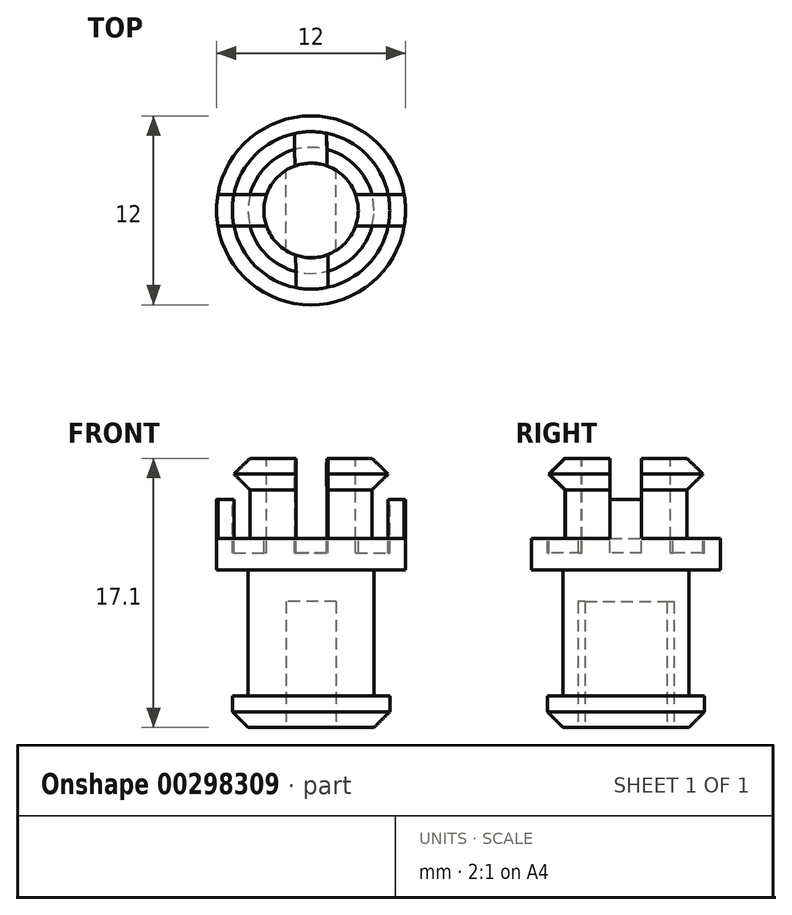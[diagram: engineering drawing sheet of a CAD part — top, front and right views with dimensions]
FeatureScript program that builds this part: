
annotation { "Feature Type Name" : "Feature", "Feature Type Description" : "" }
export const myFeature = defineFeature(function(context is Context, id is Id, definition is map)
    precondition{}
    {
        {
            var Q0;
            Q0=qCreatedBy(makeId("Top.planeOp"),FACE);
            var sketch = newSketch(context, id + "F0", { "sketchPlane" : qUnion([Q0])});
            skCircle(sketch, "E0", {"center": v(0, 0) * mm, "radius": 5 * mm});
            skSolve(sketch);
        }
        {
            var Q0;
            Q0 = qSketchRegion(id + "F0", true);
            extrude(context, id + "F1", {"entities" : qUnion([Q0]), "depth" : 2 * mm});
        }
        {
            var Q0;
            Q0=makeQuery(id+"F1.opExtrude","CAP_FACE",FACE,{"disambiguationData":[OSD([sQuery(id+"F0.wireOp",EDGE,"E0")])],"isStart":false});
            var sketch = newSketch(context, id + "F2", { "sketchPlane" : qUnion([Q0])});
            skCircle(sketch, "E1", {"center": v(0, 0) * mm, "radius": 4 * mm});
            skSolve(sketch);
        }
        {
            var Q0;
            Q0 = qSketchRegion(id + "F2", true);
            extrude(context, id + "F3", {"entities" : qUnion([Q0]), "operationType" : NewBodyOperationType.ADD, "depth" : 8 * mm});
        }
        {
            var Q0;
            Q0=makeQuery(id+"F3.opExtrude","CAP_FACE",FACE,{"disambiguationData":[OSD([sQuery(id+"F2.wireOp",EDGE,"E1")])],"isStart":false});
            var sketch = newSketch(context, id + "F4", { "sketchPlane" : qUnion([Q0])});
            skCircle(sketch, "E2", {"center": v(0, 0) * mm, "radius": 6 * mm});
            skSolve(sketch);
        }
        {
            var Q0;
            Q0 = qSketchRegion(id + "F4", true);
            extrude(context, id + "F5", {"entities" : qUnion([Q0]), "operationType" : NewBodyOperationType.ADD, "depth" : 2 * mm});
        }
        {
            var Q0;
            Q0=makeQuery(id+"F5.opExtrude","CAP_FACE",FACE,{"disambiguationData":[OSD([sQuery(id+"F4.wireOp",EDGE,"E2")])],"isStart":false});
            var sketch = newSketch(context, id + "F6", { "sketchPlane" : qUnion([Q0])});
            skCircle(sketch, "E3", {"center": v(0, 0) * mm, "radius": 4.15 * mm});
            skLineSegment(sketch, "E4", {"start": v(-5.92, 1) * mm, "end": v(-4.52, 1) * mm});
            skLineSegment(sketch, "E5.MirrorCS", {"start": v(5.92, 1) * mm, "end": v(4.52, 1) * mm});
            skLineSegment(sketch, "E6.MirrorCS", {"start": v(5.92, -1) * mm, "end": v(4.52, -1) * mm});
            skLineSegment(sketch, "E7.MirrorCS", {"start": v(-5.92, -1) * mm, "end": v(-4.52, -1) * mm});
            skLineSegment(sketch, "E8", {"start": v(-4.52, 1) * mm, "end": v(-4.52, -1) * mm});
            skLineSegment(sketch, "E9.MirrorCS", {"start": v(4.52, 1) * mm, "end": v(4.52, -1) * mm});
            skLineSegment(sketch, "E10", {"start": v(-4.03, 1) * mm, "end": v(4.03, 1) * mm});
            skLineSegment(sketch, "E11.MirrorCS", {"start": v(-4.03, -1) * mm, "end": v(4.03, -1) * mm});
            skLineSegment(sketch, "E12", {"start": v(-1, 4.03) * mm, "end": v(-1, -4.03) * mm});
            skLineSegment(sketch, "E13.MirrorCS", {"start": v(1, 4.03) * mm, "end": v(1, -4.03) * mm});
            skSolve(sketch);
        }
        {
            var Q0;
            {var subQ0=sQuery(id+"F6.wireOp",EDGE,"E5.MirrorCS");Q0=makeQuery(id+"F6.imprint","IMPRINT",FACE,{"disambiguationData":[TD([[makeQuery(id+"F6.imprint","IMPRINT",EDGE,{"derivedFrom":subQ0}),1.0]])]});}
            var Q1;
            {var subQ0=sQuery(id+"F6.wireOp",EDGE,"E4");Q1=makeQuery(id+"F6.imprint","IMPRINT",FACE,{"disambiguationData":[TD([[makeQuery(id+"F6.imprint","IMPRINT",EDGE,{"derivedFrom":subQ0}),-1.0]])]});}
            extrude(context, id + "F7", {"entities" : qUnion([Q0, Q1]), "operationType" : NewBodyOperationType.ADD, "depth" : 2.5 * mm});
        }
        {
            var Q0;
            Q0=makeQuery(id+"F5.opExtrude","CAP_FACE",FACE,{"disambiguationData":[OSD([sQuery(id+"F4.wireOp",EDGE,"E2")])],"isStart":false});
            var sketch = newSketch(context, id + "F8", { "sketchPlane" : qUnion([Q0])});
            skCircle(sketch, "E14", {"center": v(0, 0) * mm, "radius": 4 * mm});
            skCircle(sketch, "E15", {"center": v(0, 0) * mm, "radius": 3 * mm});
            skSolve(sketch);
        }
        {
            var Q0;
            Q0=makeQuery(id+"F1.opExtrude","CAP_FACE",FACE,{"disambiguationData":[OSD([sQuery(id+"F0.wireOp",EDGE,"E0")])],"isStart":true});
            var sketch = newSketch(context, id + "F9", { "sketchPlane" : qUnion([Q0])});
            skLineSegment(sketch, "E16", {"start": v(-1.6, 2.6) * mm, "end": v(-1.6, -2.6) * mm});
            skLineSegment(sketch, "E17.MirrorCS", {"start": v(1.6, 2.6) * mm, "end": v(1.6, -2.6) * mm});
            skArc(sketch, "E18", {"start": v(-1.6, 2.6) * mm, "mid": v(0, 3.05) * mm, "end": v(1.6, 2.6) * mm});
            skArc(sketch, "E19", {"start": v(-1.6, -2.6) * mm, "mid": v(0, -3.05) * mm, "end": v(1.6, -2.6) * mm});
            skSolve(sketch);
        }
        {
            var Q0;
            Q0 = qSketchRegion(id + "F9", true);
            extrude(context, id + "F10", {"entities" : qUnion([Q0]), "operationType" : NewBodyOperationType.REMOVE, "oppositeDirection" : true, "depth" : 8 * mm});
        }
        {
            var Q0;
            Q0=makeQuery(id+"F1.opExtrude","CAP_EDGE",EDGE,{"disambiguationData":[OSD([sQuery(id+"F0.wireOp",EDGE,"E0")])],"isStart":true});
            chamfer(context, id + "F11", {"entities" : qUnion([Q0]), "width" : 1 * mm, "tangentPropagation" : true});
        }
        {
            var Q0;
            Q0=makeQuery(id+"F8.imprint","IMPRINT",FACE,{"disambiguationData":[TD([[makeQuery(id+"F8.imprint","IMPRINT",EDGE,{"derivedFrom":sQuery(id+"F8.wireOp",EDGE,"E14")}),1.0]])]});
            extrude(context, id + "F12", {"entities" : qUnion([Q0]), "operationType" : NewBodyOperationType.ADD, "depth" : 3.1 * mm});
        }
        {
            var Q0;
            Q0=makeQuery(id+"F12.opExtrude","CAP_FACE",FACE,{"disambiguationData":[OSD([sQuery(id+"F8.wireOp",EDGE,"E14"),sQuery(id+"F8.wireOp",EDGE,"E15")])],"isStart":false});
            var sketch = newSketch(context, id + "F13", { "sketchPlane" : qUnion([Q0])});
            skCircle(sketch, "E20", {"center": v(0, 0) * mm, "radius": 5 * mm});
            skSolve(sketch);
        }
        {
            var Q0;
            Q0=makeQuery(id+"F13.imprint","IMPRINT",FACE,{"disambiguationData":[TD([[makeQuery(id+"F13.imprint","IMPRINT",EDGE,{"derivedFrom":sQuery(id+"F13.wireOp",EDGE,"E20")}),1.0]])]});
            var Q1;
            Q1=makeQuery(id+"F13.imprint","IMPRINT",FACE,{"disambiguationData":[TD([[makeQuery(id+"F13.imprint","IMPRINT",EDGE,{"derivedFrom":makeQuery(id+"F12.opExtrude","CAP_EDGE",EDGE,{"disambiguationData":[OSD([sQuery(id+"F8.wireOp",EDGE,"E14")])],"isStart":false})}),1.0]])]});
            extrude(context, id + "F14", {"entities" : qUnion([Q0, Q1]), "operationType" : NewBodyOperationType.ADD, "depth" : 2 * mm});
        }
        {
            var Q0;
            Q0=makeQuery(id+"F14.opExtrude","CAP_FACE",FACE,{"disambiguationData":[OSD([sQuery(id+"F8.wireOp",EDGE,"E15"),sQuery(id+"F13.wireOp",EDGE,"E20")])],"isStart":false});
            var sketch = newSketch(context, id + "F15", { "sketchPlane" : qUnion([Q0])});
            skLineSegment(sketch, "E21", {"start": v(-4.9, 1) * mm, "end": v(4.9, 1) * mm});
            skLineSegment(sketch, "E22.MirrorCS", {"start": v(-4.9, -1) * mm, "end": v(4.9, -1) * mm});
            skLineSegment(sketch, "E23", {"start": v(-1.05, 4.89) * mm, "end": v(-0.95, -4.9) * mm});
            skLineSegment(sketch, "E24.MirrorCS", {"start": v(1, 4.9) * mm, "end": v(1.08, -4.89) * mm});
            skSolve(sketch);
        }
        {
            var Q0;
            {var subQ0=sQuery(id+"F15.wireOp",EDGE,"E21");var subQ1=makeQuery(id+"F14.opExtrude","CAP_EDGE",EDGE,{"disambiguationData":[OSD([sQuery(id+"F13.wireOp",EDGE,"E20")])],"isStart":false});var subQ2=makeQuery(id+"F15.imprint","INTERSECT",VERTEX,{"disambiguationData":[OD(1.0)],"derivedFrom":[subQ1,subQ0]});Q0=makeQuery(id+"F15.imprint","IMPRINT",FACE,{"disambiguationData":[TD([[makeQuery(id+"F15.imprint","IMPRINT",EDGE,{"disambiguationData":[TD([[subQ2,1.0]])],"derivedFrom":subQ0}),-1.0]])]});}
            var Q1;
            {var subQ0=sQuery(id+"F15.wireOp",EDGE,"E23");var subQ1=makeQuery(id+"F14.opExtrude","CAP_EDGE",EDGE,{"disambiguationData":[OSD([sQuery(id+"F13.wireOp",EDGE,"E20")])],"isStart":false});var subQ2=makeQuery(id+"F15.imprint","INTERSECT",VERTEX,{"disambiguationData":[OD(0.0)],"derivedFrom":[subQ1,subQ0]});Q1=makeQuery(id+"F15.imprint","IMPRINT",FACE,{"disambiguationData":[TD([[makeQuery(id+"F15.imprint","IMPRINT",EDGE,{"disambiguationData":[TD([[subQ2,-1.0]])],"derivedFrom":subQ0}),1.0]])]});}
            var Q2;
            {var subQ0=sQuery(id+"F15.wireOp",EDGE,"E21");var subQ1=makeQuery(id+"F14.opExtrude","CAP_EDGE",EDGE,{"disambiguationData":[OSD([sQuery(id+"F13.wireOp",EDGE,"E20")])],"isStart":false});var subQ2=makeQuery(id+"F15.imprint","INTERSECT",VERTEX,{"disambiguationData":[OD(0.0)],"derivedFrom":[subQ1,subQ0]});Q2=makeQuery(id+"F15.imprint","IMPRINT",FACE,{"disambiguationData":[TD([[makeQuery(id+"F15.imprint","IMPRINT",EDGE,{"disambiguationData":[TD([[subQ2,-1.0]])],"derivedFrom":subQ0}),-1.0]])]});}
            var Q3;
            {var subQ0=sQuery(id+"F15.wireOp",EDGE,"E23");var subQ1=makeQuery(id+"F14.opExtrude","CAP_EDGE",EDGE,{"disambiguationData":[OSD([sQuery(id+"F13.wireOp",EDGE,"E20")])],"isStart":false});var subQ2=makeQuery(id+"F15.imprint","INTERSECT",VERTEX,{"disambiguationData":[OD(1.0)],"derivedFrom":[subQ1,subQ0]});Q3=makeQuery(id+"F15.imprint","IMPRINT",FACE,{"disambiguationData":[TD([[makeQuery(id+"F15.imprint","IMPRINT",EDGE,{"disambiguationData":[TD([[subQ2,1.0]])],"derivedFrom":subQ0}),1.0]])]});}
            extrude(context, id + "F16", {"entities" : qUnion([Q0, Q1, Q2, Q3]), "operationType" : NewBodyOperationType.REMOVE, "oppositeDirection" : true, "depth" : 6 * mm});
        }
        {
            var Q0;
            {var subQ0=sQuery(id+"F13.wireOp",EDGE,"E20");var subQ2=sQuery(id+"F15.wireOp",EDGE,"E22.MirrorCS");var subQ3=makeQuery(id+"F14.opExtrude","CAP_EDGE",EDGE,{"disambiguationData":[OSD([subQ0])],"isStart":false});Q0=makeQuery(id+"F16.boolean.opBoolean","SPLIT",EDGE,{"disambiguationData":[TD([makeQuery(id+"F16.opExtrude","SWEPT_FACE",FACE,{"disambiguationData":[OSD([subQ2]),TDD([makeQuery(id+"F15.imprint","IMPRINT",EDGE,{"disambiguationData":[TD([[makeQuery(id+"F15.imprint","INTERSECT",VERTEX,{"disambiguationData":[OD(1.0)],"derivedFrom":[subQ3,subQ2]}),1.0]])],"derivedFrom":subQ2})])]})])],"derivedFrom":makeQuery(id+"F14.opExtrude","CAP_EDGE",EDGE,{"disambiguationData":[OSD([subQ0])],"isStart":true})});}
            var Q1;
            {var subQ0=sQuery(id+"F13.wireOp",EDGE,"E20");var subQ2=sQuery(id+"F15.wireOp",EDGE,"E21");var subQ3=makeQuery(id+"F14.opExtrude","CAP_EDGE",EDGE,{"disambiguationData":[OSD([subQ0])],"isStart":false});Q1=makeQuery(id+"F16.boolean.opBoolean","SPLIT",EDGE,{"disambiguationData":[TD([makeQuery(id+"F16.opExtrude","SWEPT_FACE",FACE,{"disambiguationData":[OSD([subQ2]),TDD([makeQuery(id+"F15.imprint","IMPRINT",EDGE,{"disambiguationData":[TD([[makeQuery(id+"F15.imprint","INTERSECT",VERTEX,{"disambiguationData":[OD(1.0)],"derivedFrom":[subQ3,subQ2]}),1.0]])],"derivedFrom":subQ2})])]})])],"derivedFrom":makeQuery(id+"F14.opExtrude","CAP_EDGE",EDGE,{"disambiguationData":[OSD([subQ0])],"isStart":true})});}
            var Q2;
            {var subQ0=sQuery(id+"F13.wireOp",EDGE,"E20");var subQ1=sQuery(id+"F15.wireOp",EDGE,"E22.MirrorCS");var subQ2=makeQuery(id+"F14.opExtrude","CAP_EDGE",EDGE,{"disambiguationData":[OSD([subQ0])],"isStart":false});Q2=makeQuery(id+"F16.boolean.opBoolean","SPLIT",EDGE,{"disambiguationData":[TD([makeQuery(id+"F16.opExtrude","SWEPT_FACE",FACE,{"disambiguationData":[OSD([subQ1]),TDD([makeQuery(id+"F15.imprint","IMPRINT",EDGE,{"disambiguationData":[TD([[makeQuery(id+"F15.imprint","INTERSECT",VERTEX,{"disambiguationData":[OD(0.0)],"derivedFrom":[subQ2,subQ1]}),-1.0]])],"derivedFrom":subQ1})])]})])],"derivedFrom":makeQuery(id+"F14.opExtrude","CAP_EDGE",EDGE,{"disambiguationData":[OSD([subQ0])],"isStart":true})});}
            var Q3;
            {var subQ0=sQuery(id+"F13.wireOp",EDGE,"E20");var subQ2=sQuery(id+"F15.wireOp",EDGE,"E22.MirrorCS");var subQ3=makeQuery(id+"F14.opExtrude","CAP_EDGE",EDGE,{"disambiguationData":[OSD([subQ0])],"isStart":false});Q3=makeQuery(id+"F16.boolean.opBoolean","SPLIT",EDGE,{"disambiguationData":[TD([makeQuery(id+"F16.opExtrude","SWEPT_FACE",FACE,{"disambiguationData":[OSD([subQ2]),TDD([makeQuery(id+"F15.imprint","IMPRINT",EDGE,{"disambiguationData":[TD([[makeQuery(id+"F15.imprint","INTERSECT",VERTEX,{"disambiguationData":[OD(1.0)],"derivedFrom":[subQ3,subQ2]}),1.0]])],"derivedFrom":subQ2})])]})])],"derivedFrom":subQ3});}
            var Q4;
            {var subQ0=sQuery(id+"F13.wireOp",EDGE,"E20");var subQ1=sQuery(id+"F15.wireOp",EDGE,"E22.MirrorCS");var subQ2=makeQuery(id+"F14.opExtrude","CAP_EDGE",EDGE,{"disambiguationData":[OSD([subQ0])],"isStart":false});Q4=makeQuery(id+"F16.boolean.opBoolean","SPLIT",EDGE,{"disambiguationData":[TD([makeQuery(id+"F16.opExtrude","SWEPT_FACE",FACE,{"disambiguationData":[OSD([subQ1]),TDD([makeQuery(id+"F15.imprint","IMPRINT",EDGE,{"disambiguationData":[TD([[makeQuery(id+"F15.imprint","INTERSECT",VERTEX,{"disambiguationData":[OD(0.0)],"derivedFrom":[subQ2,subQ1]}),-1.0]])],"derivedFrom":subQ1})])]})])],"derivedFrom":subQ2});}
            var Q5;
            {var subQ0=sQuery(id+"F13.wireOp",EDGE,"E20");var subQ2=sQuery(id+"F15.wireOp",EDGE,"E21");var subQ3=makeQuery(id+"F14.opExtrude","CAP_EDGE",EDGE,{"disambiguationData":[OSD([subQ0])],"isStart":false});Q5=makeQuery(id+"F16.boolean.opBoolean","SPLIT",EDGE,{"disambiguationData":[TD([makeQuery(id+"F16.opExtrude","SWEPT_FACE",FACE,{"disambiguationData":[OSD([subQ2]),TDD([makeQuery(id+"F15.imprint","IMPRINT",EDGE,{"disambiguationData":[TD([[makeQuery(id+"F15.imprint","INTERSECT",VERTEX,{"disambiguationData":[OD(1.0)],"derivedFrom":[subQ3,subQ2]}),1.0]])],"derivedFrom":subQ2})])]})])],"derivedFrom":subQ3});}
            var Q6;
            {var subQ0=sQuery(id+"F13.wireOp",EDGE,"E20");var subQ3=makeQuery(id+"F14.opExtrude","CAP_EDGE",EDGE,{"disambiguationData":[OSD([subQ0])],"isStart":false});var subQ5=sQuery(id+"F15.wireOp",EDGE,"E21");Q6=makeQuery(id+"F16.boolean.opBoolean","SPLIT",EDGE,{"disambiguationData":[TD([makeQuery(id+"F16.opExtrude","SWEPT_FACE",FACE,{"disambiguationData":[OSD([subQ5]),TDD([makeQuery(id+"F15.imprint","IMPRINT",EDGE,{"disambiguationData":[TD([[makeQuery(id+"F15.imprint","INTERSECT",VERTEX,{"disambiguationData":[OD(0.0)],"derivedFrom":[subQ3,subQ5]}),-1.0]])],"derivedFrom":subQ5})])]})])],"derivedFrom":subQ3});}
            var Q7;
            {var subQ0=sQuery(id+"F13.wireOp",EDGE,"E20");var subQ2=sQuery(id+"F15.wireOp",EDGE,"E21");var subQ3=makeQuery(id+"F14.opExtrude","CAP_EDGE",EDGE,{"disambiguationData":[OSD([subQ0])],"isStart":false});Q7=makeQuery(id+"F16.boolean.opBoolean","SPLIT",EDGE,{"disambiguationData":[TD([makeQuery(id+"F16.opExtrude","SWEPT_FACE",FACE,{"disambiguationData":[OSD([subQ2]),TDD([makeQuery(id+"F15.imprint","IMPRINT",EDGE,{"disambiguationData":[TD([[makeQuery(id+"F15.imprint","INTERSECT",VERTEX,{"disambiguationData":[OD(0.0)],"derivedFrom":[subQ3,subQ2]}),-1.0]])],"derivedFrom":subQ2})])]})])],"derivedFrom":makeQuery(id+"F14.opExtrude","CAP_EDGE",EDGE,{"disambiguationData":[OSD([subQ0])],"isStart":true})});}
            chamfer(context, id + "F17", {"entities" : qUnion([Q0, Q1, Q2, Q3, Q4, Q5, Q6, Q7]), "width" : 1 * mm, "tangentPropagation" : true});
        }
    });
